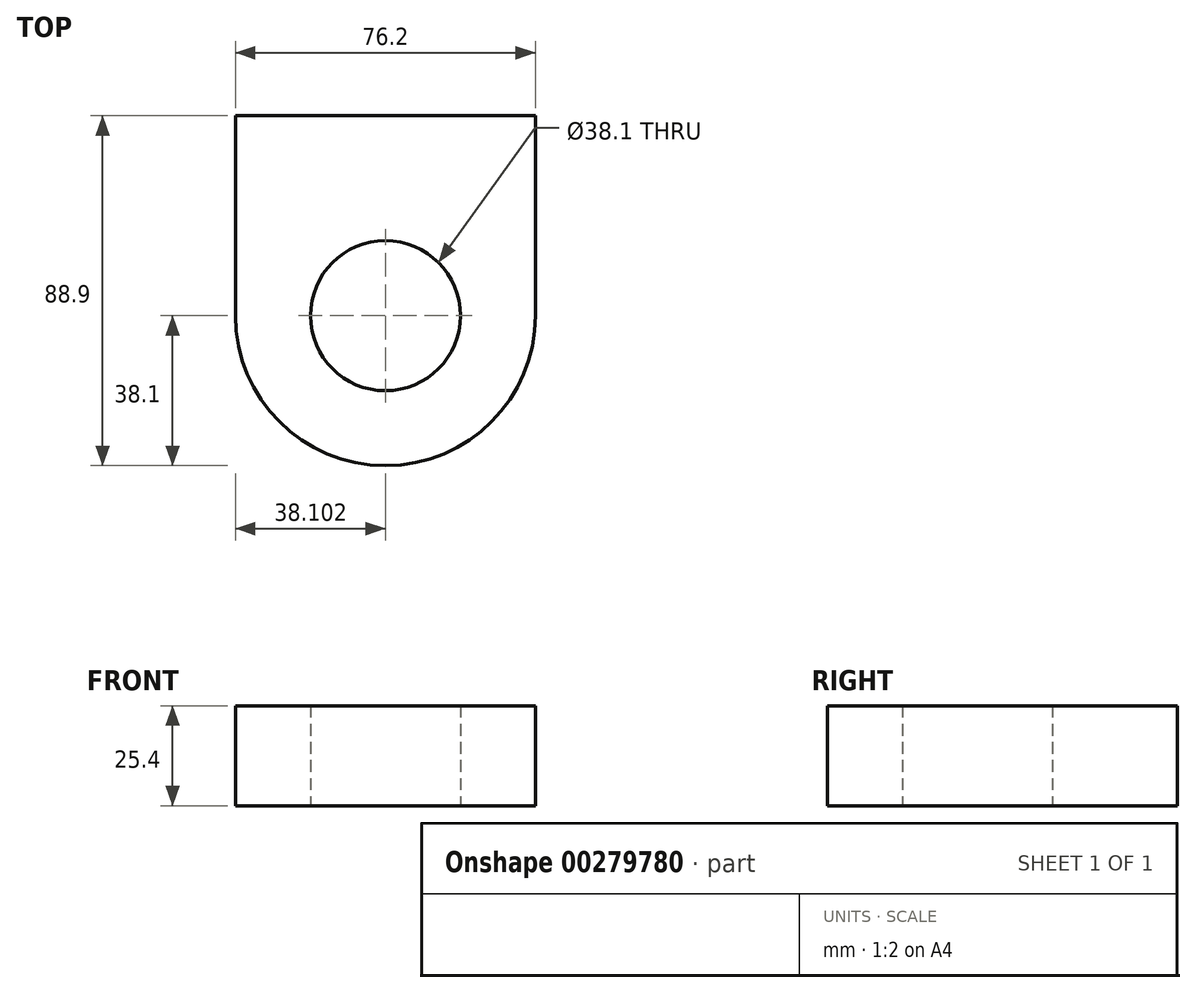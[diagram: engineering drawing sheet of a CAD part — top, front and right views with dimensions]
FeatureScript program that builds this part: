
annotation { "Feature Type Name" : "Feature", "Feature Type Description" : "" }
export const myFeature = defineFeature(function(context is Context, id is Id, definition is map)
    precondition{}
    {
        {
            var Q0;
            Q0=qCreatedBy(makeId("Top.planeOp"),FACE);
            var sketch = newSketch(context, id + "F0", { "sketchPlane" : qUnion([Q0])});
            skLineSegment(sketch, "E0", {"start": v(-51.1, 0) * mm, "end": v(-51.1, 50.8) * mm});
            skLineSegment(sketch, "E1", {"start": v(-51.1, 50.8) * mm, "end": v(25.1, 50.8) * mm});
            skLineSegment(sketch, "E2", {"start": v(25.1, 50.8) * mm, "end": v(25.1, 0) * mm});
            skArc(sketch, "E3", {"start": v(-51.1, 0) * mm, "mid": v(-13, -38.1) * mm, "end": v(25.1, 0) * mm});
            skCircle(sketch, "E4", {"center": v(-13, 0) * mm, "radius": 19.05 * mm});
            skSolve(sketch);
        }
        {
            var Q0;
            Q0=makeQuery(id+"F0.imprint","IMPRINT",FACE,{"disambiguationData":[TD([[makeQuery(id+"F0.imprint","IMPRINT",EDGE,{"derivedFrom":sQuery(id+"F0.wireOp",EDGE,"E0")}),-1.0]])]});
            extrude(context, id + "F1", {"entities" : qUnion([Q0]), "depth" : 25.4 * mm});
        }
    });
